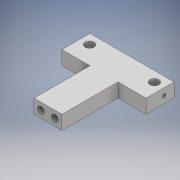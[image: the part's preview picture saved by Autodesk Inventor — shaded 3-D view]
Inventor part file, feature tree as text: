
AUTODESK INVENTOR PART (.ipt)
format: ipt  version: 2017.3 (Build 213256000, 256)  size: 137,216 bytes
history: native  units: mm
features: sketch x7, extrude x4, hole x3
ambient origin geometry x8: Origin, YZ Plane, XZ Plane, XY Plane, X Axis, Y Axis, Z Axis, Center Point
bodies: Solid1 (feature_tree)
feature tree (14):
  extrude  "Extrusion1"  Depth=20.0mm
  extrude  "Extrusion3"  Depth=10.0mm TaperAngle=0.0deg
  extrude  "Extrusion4"  Depth=3.175mm
  sketch  "Sketch6"  dims[d12=5.0mm d13=0.0mm]
  sketch  "Sketch7"  dims[d21=1.221mm d22=3.0mm d23=4.0mm d24=2.0mm d25=90.0deg d26=3.0mm d27=20.594885mm]
  hole  "Hole2"  [1 undecoded]
  hole  "Hole3"  [1 undecoded]
  extrude  "Extrusion5"  [1 undecoded]
  hole  "Hole4"  [1 undecoded]
  sketch  "Sketch1"  dims[d0=30.0mm d1=20.0mm]
  sketch  "Sketch4"  dims[d2=5.0mm d3=0.0mm d8=10.0mm d9=0.0mm]
  sketch  "Sketch5"  dims[d10=3.175mm d11=3.175mm]
  sketch  "Sketch9"  dims[d28=1.221mm d29=3.0mm d30=4.0mm d31=2.0mm d32=90.0deg d33=3.0mm d34=20.594885mm d35=10.0mm]
  sketch  "Sketch10"  dims[d36=5.0mm d37=20.0mm d38=0.0mm d39=2.487mm d40=10.0mm d41=4.0mm d42=2.0mm d43=90.0deg d44=10.0mm d45=20.594885mm]
note: 4 required parameter values undecoded (feature->parameter linkage not recoverable at this tier; creation-order binding heuristic only, values carry confidence <= 0.55)
